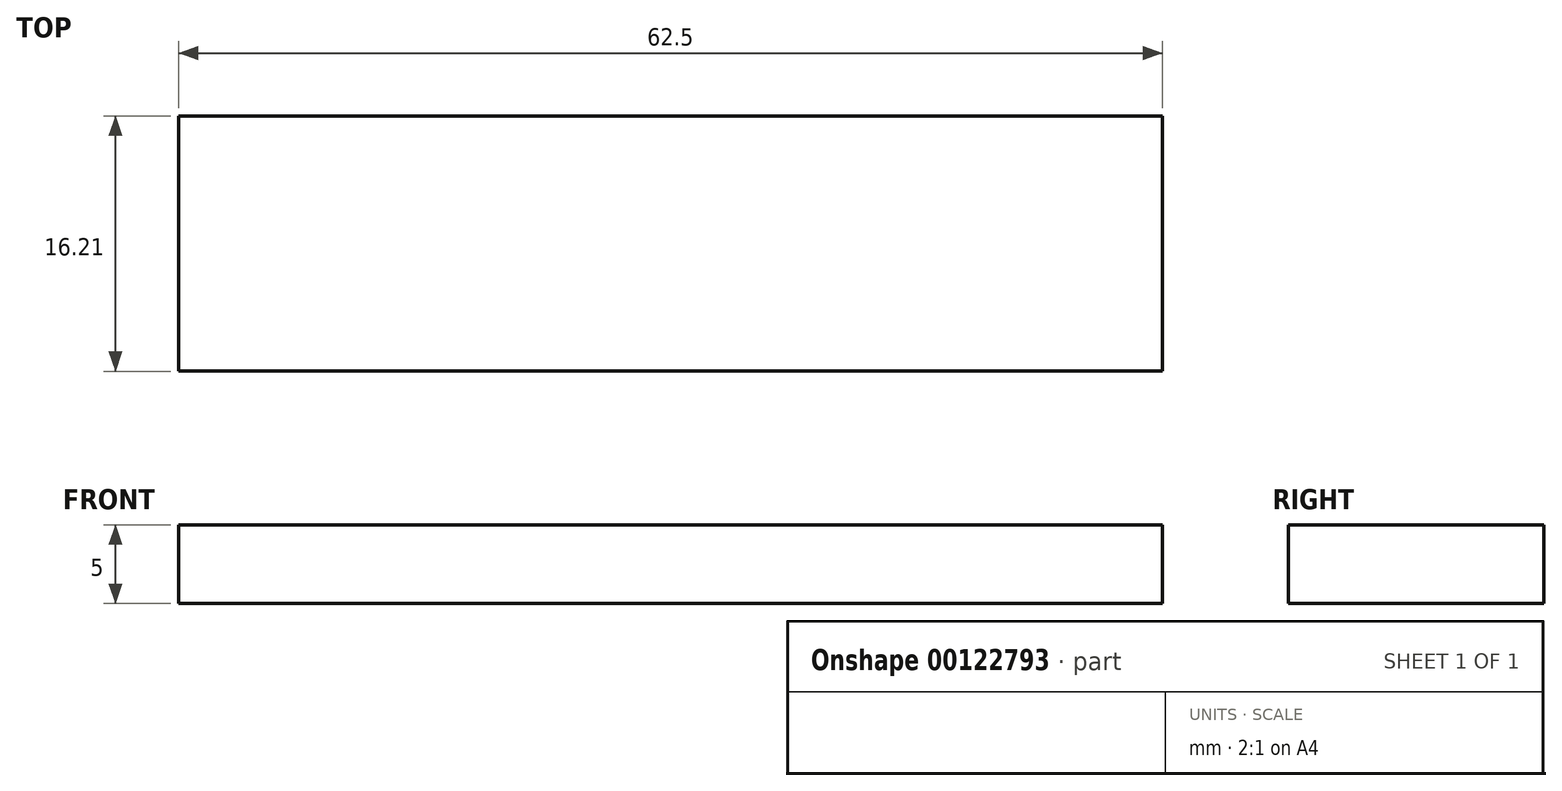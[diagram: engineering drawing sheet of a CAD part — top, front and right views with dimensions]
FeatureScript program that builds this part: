
annotation { "Feature Type Name" : "Feature", "Feature Type Description" : "" }
export const myFeature = defineFeature(function(context is Context, id is Id, definition is map)
    precondition{}
    {
        {
            var Q0;
            Q0=qCreatedBy(makeId("Top.planeOp"),FACE);
            var sketch = newSketch(context, id + "F0", { "sketchPlane" : qUnion([Q0])});
            skLineSegment(sketch, "E0.bottom", {"start": v(-46, -15.48) * mm, "end": v(16.5, -15.48) * mm});
            skLineSegment(sketch, "E0.top", {"start": v(-46, -31.69) * mm, "end": v(16.5, -31.69) * mm});
            skLineSegment(sketch, "E0.left", {"start": v(-46, -15.48) * mm, "end": v(-46, -31.69) * mm});
            skLineSegment(sketch, "E0.right", {"start": v(16.5, -15.48) * mm, "end": v(16.5, -31.69) * mm});
            skSolve(sketch);
        }
        {
            var Q0;
            Q0 = qSketchRegion(id + "F0", true);
            var Q1;
            Q1=makeQuery(id+"F0.imprint","IMPRINT",FACE,{"disambiguationData":[TD([[makeQuery(id+"F0.imprint","IMPRINT",EDGE,{"derivedFrom":sQuery(id+"F0.wireOp",EDGE,"E0.bottom")}),-1.0]])]});
            extrude(context, id + "F1", {"entities" : qUnion([Q0, Q1]), "oppositeDirection" : true, "depth" : 5 * mm});
        }
    });
